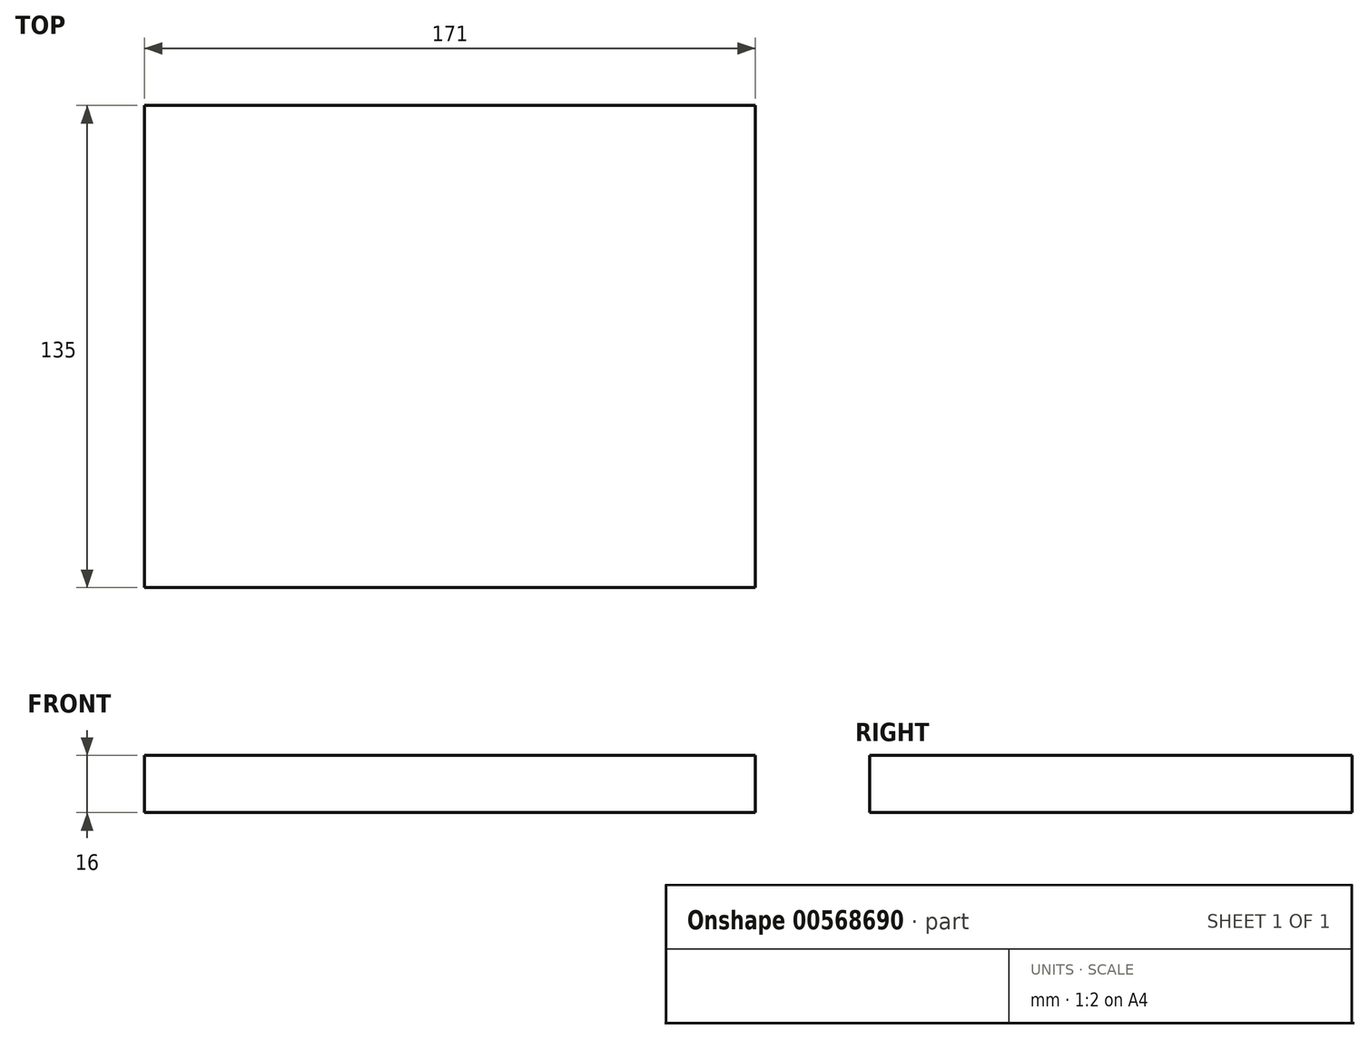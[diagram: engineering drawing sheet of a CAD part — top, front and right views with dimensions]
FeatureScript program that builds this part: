
annotation { "Feature Type Name" : "Feature", "Feature Type Description" : "" }
export const myFeature = defineFeature(function(context is Context, id is Id, definition is map)
    precondition{}
    {
        {
            var Q0;
            Q0=qCreatedBy(makeId("Top.planeOp"),FACE);
            var sketch = newSketch(context, id + "F0", { "sketchPlane" : qUnion([Q0])});
            skLineSegment(sketch, "E0.bottom", {"start": v(-85.5, -67.5) * mm, "end": v(85.5, -67.5) * mm});
            skLineSegment(sketch, "E0.top", {"start": v(-85.5, 67.5) * mm, "end": v(85.5, 67.5) * mm});
            skLineSegment(sketch, "E0.left", {"start": v(-85.5, -67.5) * mm, "end": v(-85.5, 67.5) * mm});
            skLineSegment(sketch, "E0.right", {"start": v(85.5, -67.5) * mm, "end": v(85.5, 67.5) * mm});
            skPoint(sketch, "E0.middle", {"position": v(0, 0) * mm});
            skSolve(sketch);
        }
        {
            var Q0;
            Q0=makeQuery(id+"F0.imprint","IMPRINT",FACE,{"disambiguationData":[TD([[makeQuery(id+"F0.imprint","IMPRINT",EDGE,{"derivedFrom":sQuery(id+"F0.wireOp",EDGE,"E0.bottom")}),1.0]])]});
            extrude(context, id + "F1", {"entities" : qUnion([Q0]), "depth" : 16 * mm, "offsetDistance" : 25 * mm});
        }
    });
